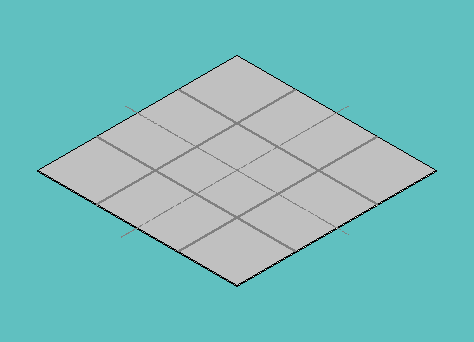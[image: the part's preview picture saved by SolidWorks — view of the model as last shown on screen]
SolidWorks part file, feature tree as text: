
SOLIDWORKS PART (.sldprt)
format: sldprt  version: not decoded by parser v0  size: 260,608 bytes
history: native  units: mm
features: plane x6, sketch x5, extrude x2, material x1 (+11 scaffold rows collapsed)
feature tree (25):
  scaffold x11  (default folders/planes/origin — collapsed)
  material  "Material <not specified>"
  sketch  "Sketch1"  dims[D1=609.6mm D2=609.6mm]
  extrude  "Extrude1"  Depth=3.175mm
  plane  "fwd right"  Offset=119.717896mm
  plane  "fwd left"  Offset=119.717896mm
  plane  "fwd ref plane"  Offset=101.6mm
  plane  "strafe front"  Offset=119.518659mm
  plane  "strafe back"  Offset=119.518659mm
  plane  "strafe ref plane"  Offset=101.6mm
  sketch  "straight path"  dims[c1.D1=~479.789027mm c1.D2=~119.717896mm c1.D3=~119.717896mm c1.D4=~69.40042mm c1.D5=~69.40042mm c2.D1=~119.518659mm c2.D4=~119.518659mm]
  sketch  "strafe path"  dims[c1.D1=~479.789027mm c1.D2=~119.717896mm c1.D3=~119.717896mm c1.D4=~69.40042mm c1.D5=~69.40042mm c2.D1=~119.518659mm c2.D4=~119.518659mm]
  sketch  "sketch3"  dims[D1=351.5233mm D2=25.4mm]
  sketch  "curved path"  dims[D1=~351.523146mm]
  extrude  "Extrude2"  Depth=25.4mm
decode coverage: 7 of 7 modeling features carry decoded parameters
note: ~ marks probable driven/reference dimensions
note: suppression state not decoded; provenance and decode notes live in map.json
